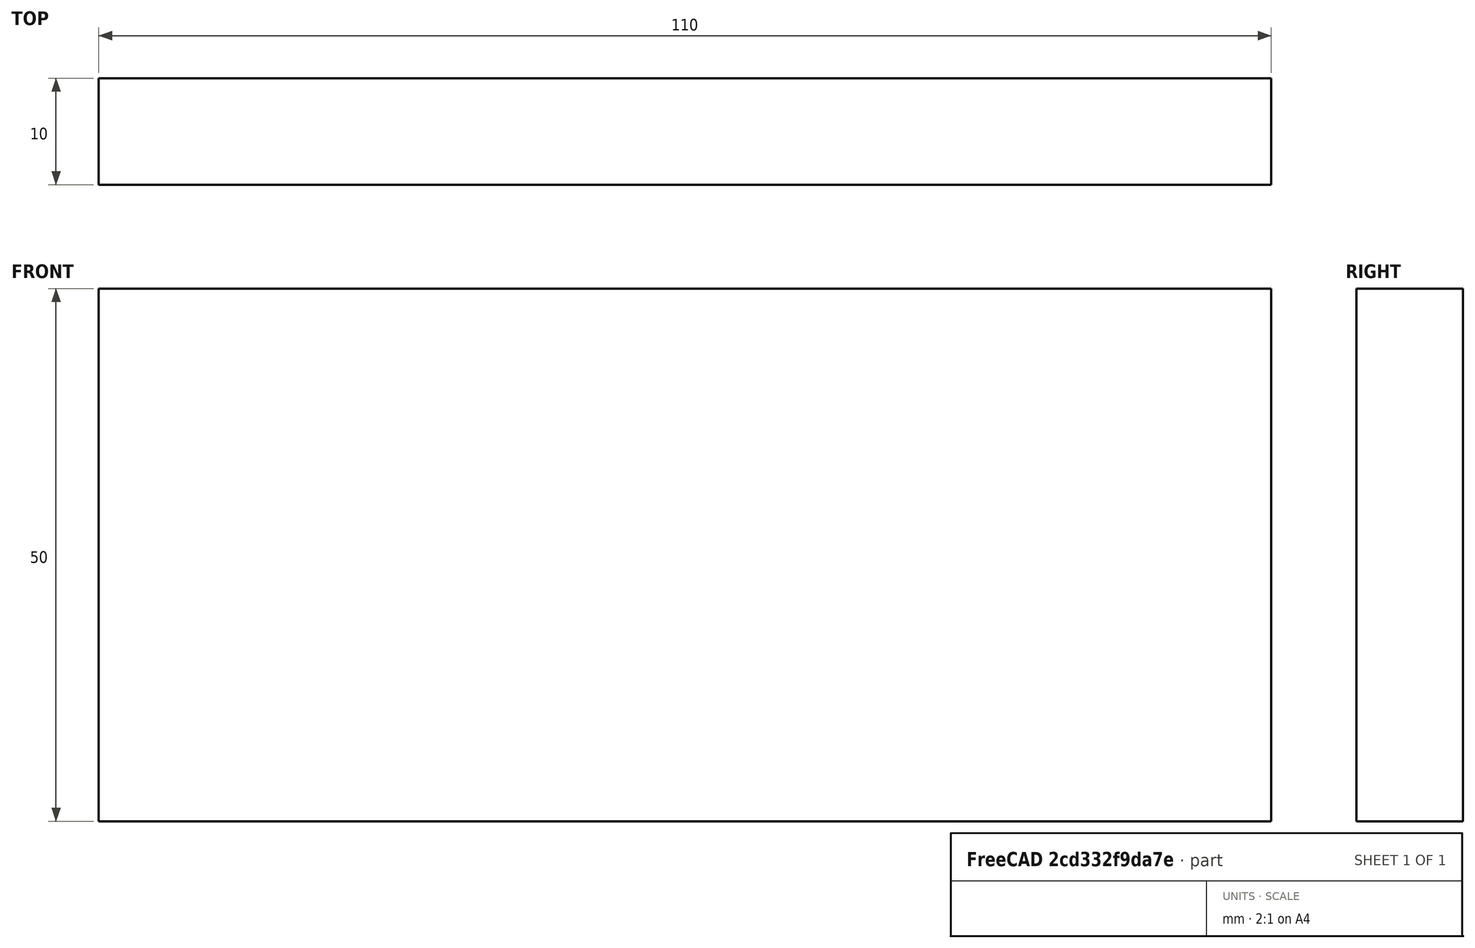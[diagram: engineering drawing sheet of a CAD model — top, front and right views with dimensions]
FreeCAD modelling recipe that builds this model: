
FCSTD DOCUMENT  (FreeCAD 0.15R4671 (Git))
Label: Flat Bar 110x10 EN10058 S235JR
License: All rights reserved
LicenseURL: http://en.wikipedia.org/wiki/All_rights_reserved
objects: Sketcher::SketchObject×1, Part::Extrusion×1
note: 2 computed .brp shape members not serialized (recipe doc carries the construction recipe); baked Part::Feature solids carry a one-line shape summary decoded from their .brp

FEATURE [Sketcher::SketchObject] Sketch
  sketch-geometry (4):
    g0: LineSegment StartX=-55 StartY=-5 StartZ=0 EndX=55 EndY=-5 EndZ=0
    g1: LineSegment StartX=55 StartY=-5 StartZ=0 EndX=55 EndY=5 EndZ=0
    g2: LineSegment StartX=55 StartY=5 StartZ=0 EndX=-55 EndY=5 EndZ=0
    g3: LineSegment StartX=-55 StartY=5 StartZ=0 EndX=-55 EndY=-5 EndZ=0
  constraints (12):
    c: Coincident(g0,g1)
    c: Coincident(g1,g2)
    c: Coincident(g2,g3)
    c: Coincident(g3,g0)
    c: Horizontal(g0)
    c: Horizontal(g2)
    c: Vertical(g1)
    c: Vertical(g3)
    c: Symmetric(g1,g2,g-2)
    c: Symmetric(g0,g1,g-1)
    c: DistanceY(g1) = 10
    c: DistanceX(g0) = 110
FEATURE [Part::Extrusion] Extrude  label="Flat Bar 110x10 EN10058 S235JR"
  Base = -> Sketch
  Dir = (0,0,50)
  Solid = true
